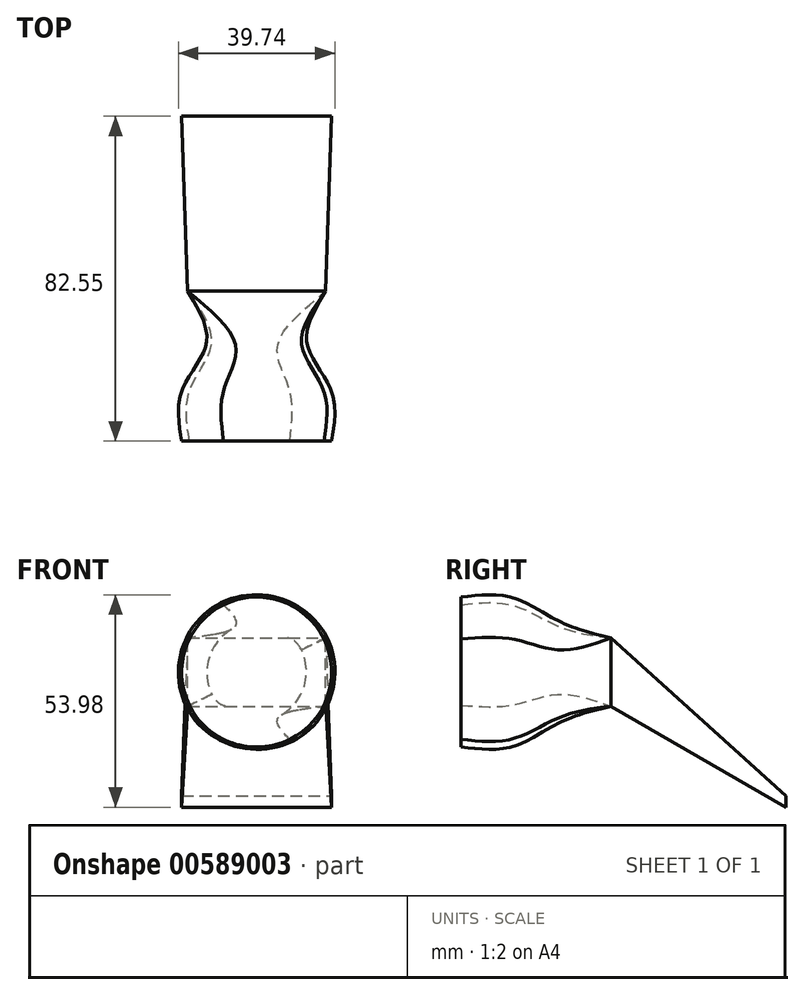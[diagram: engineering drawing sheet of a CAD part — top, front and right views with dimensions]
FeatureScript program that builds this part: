
annotation { "Feature Type Name" : "Feature", "Feature Type Description" : "" }
export const myFeature = defineFeature(function(context is Context, id is Id, definition is map)
    precondition{}
    {
        {
            var Q0;
            Q0=qCreatedBy(makeId("Front.planeOp"),FACE);
            var sketch = newSketch(context, id + "F0", { "sketchPlane" : qUnion([Q0])});
            skCircle(sketch, "E0", {"center": v(0, 0) * mm, "radius": 19.05 * mm});
            skSolve(sketch);
        }
        {
            var Q0;
            Q0=qCreatedBy(makeId("Front.planeOp"),FACE);
            cPlane(context, id + "F1", {"entities" : qUnion([Q0]), "cplaneType" : CPlaneType.OFFSET, "offset" : 12.7 * mm, "width" : 152.4 * mm, "height" : 152.4 * mm});
        }
        {
            var Q0;
            Q0=qCreatedBy(id+"F1.planeOp",FACE);
            var sketch = newSketch(context, id + "F2", { "sketchPlane" : qUnion([Q0])});
            skCircle(sketch, "E1", {"center": v(0, 0) * mm, "radius": 19.05 * mm});
            skSolve(sketch);
        }
        {
            var Q0;
            Q0=qCreatedBy(makeId("Front.planeOp"),FACE);
            cPlane(context, id + "F3", {"entities" : qUnion([Q0]), "cplaneType" : CPlaneType.OFFSET, "offset" : 12.7 * mm, "oppositeDirection" : true, "width" : 152.4 * mm, "height" : 152.4 * mm});
        }
        {
            var Q0;
            Q0=qCreatedBy(id+"F3.planeOp",FACE);
            var sketch = newSketch(context, id + "F4", { "sketchPlane" : qUnion([Q0])});
            skCircle(sketch, "E2", {"center": v(0, 0) * mm, "radius": 12.7 * mm});
            skSolve(sketch);
        }
        {
            var Q0;
            Q0=qCreatedBy(id+"F3.planeOp",FACE);
            cPlane(context, id + "F5", {"entities" : qUnion([Q0]), "cplaneType" : CPlaneType.OFFSET, "offset" : 12.7 * mm, "oppositeDirection" : true, "width" : 152.4 * mm, "height" : 152.4 * mm});
        }
        {
            var Q0;
            Q0=qCreatedBy(id+"F5.planeOp",FACE);
            var sketch = newSketch(context, id + "F6", { "sketchPlane" : qUnion([Q0])});
            skLineSegment(sketch, "E3.bottom", {"start": v(-17.54, -8.67) * mm, "end": v(17.54, -8.67) * mm});
            skLineSegment(sketch, "E3.top", {"start": v(-17.54, 8.67) * mm, "end": v(17.54, 8.67) * mm});
            skLineSegment(sketch, "E3.left", {"start": v(-17.54, -8.67) * mm, "end": v(-17.54, 8.67) * mm});
            skLineSegment(sketch, "E3.right", {"start": v(17.54, -8.67) * mm, "end": v(17.54, 8.67) * mm});
            skPoint(sketch, "E3.middle", {"position": v(0, 0) * mm});
            skSolve(sketch);
        }
        {
            var Q0;
            Q0=qCreatedBy(id+"F5.planeOp",FACE);
            cPlane(context, id + "F7", {"entities" : qUnion([Q0]), "cplaneType" : CPlaneType.OFFSET, "offset" : 44.45 * mm, "oppositeDirection" : true, "width" : 152.4 * mm, "height" : 152.4 * mm});
        }
        {
            var Q0;
            Q0=qCreatedBy(id+"F7.planeOp",FACE);
            var sketch = newSketch(context, id + "F8", { "sketchPlane" : qUnion([Q0])});
            skLineSegment(sketch, "E4.bottom", {"start": v(-19.05, -34.33) * mm, "end": v(19.05, -34.33) * mm});
            skLineSegment(sketch, "E4.top", {"start": v(-19.05, -31.42) * mm, "end": v(19.05, -31.42) * mm});
            skLineSegment(sketch, "E4.left", {"start": v(-19.05, -34.33) * mm, "end": v(-19.05, -31.42) * mm});
            skLineSegment(sketch, "E4.right", {"start": v(19.05, -34.33) * mm, "end": v(19.05, -31.42) * mm});
            skPoint(sketch, "E4.middle", {"position": v(0, -32.87) * mm});
            skSolve(sketch);
        }
        {
            var Q0;
            Q0=makeQuery(id+"F2.imprint","IMPRINT",FACE,{"disambiguationData":[TD([[makeQuery(id+"F2.imprint","IMPRINT",EDGE,{"derivedFrom":sQuery(id+"F2.wireOp",EDGE,"E1")}),1.0]])]});
            var Q1;
            Q1=makeQuery(id+"F0.imprint","IMPRINT",FACE,{"disambiguationData":[TD([[makeQuery(id+"F0.imprint","IMPRINT",EDGE,{"derivedFrom":sQuery(id+"F0.wireOp",EDGE,"E0")}),1.0]])]});
            var Q2;
            Q2=makeQuery(id+"F4.imprint","IMPRINT",FACE,{"disambiguationData":[TD([[makeQuery(id+"F4.imprint","IMPRINT",EDGE,{"derivedFrom":sQuery(id+"F4.wireOp",EDGE,"E2")}),1.0]])]});
            var Q3;
            Q3=makeQuery(id+"F6.imprint","IMPRINT",FACE,{"disambiguationData":[TD([[makeQuery(id+"F6.imprint","IMPRINT",EDGE,{"derivedFrom":sQuery(id+"F6.wireOp",EDGE,"E3.bottom")}),1.0]])]});
            loft(context, id + "F9", {"sheetProfilesArray" : [{ "sheetProfileEntities" : qUnion([Q0]) }, { "sheetProfileEntities" : qUnion([Q1]) }, { "sheetProfileEntities" : qUnion([Q2]) }, { "sheetProfileEntities" : qUnion([Q3]) }]});
        }
        {
            var Q1;
            Q1=makeQuery(id+"F9.opLoft","CAP_FACE",FACE,{"disambiguationData":[OSD([makeQuery(id+"F6.imprint","IMPRINT",FACE,{"disambiguationData":[TD([[makeQuery(id+"F6.imprint","IMPRINT",EDGE,{"derivedFrom":sQuery(id+"F6.wireOp",EDGE,"E3.bottom")}),1.0]])]})])],"isStart":true});
            var Q2;
            Q2=makeQuery(id+"F8.imprint","IMPRINT",FACE,{"disambiguationData":[TD([[makeQuery(id+"F8.imprint","IMPRINT",EDGE,{"derivedFrom":sQuery(id+"F8.wireOp",EDGE,"E4.bottom")}),1.0]])]});
            loft(context, id + "F10", {"operationType" : NewBodyOperationType.ADD, "sheetProfilesArray" : [{ "sheetProfileEntities" : qUnion([Q1]) }, { "sheetProfileEntities" : qUnion([Q2]) }]});
        }
    });
